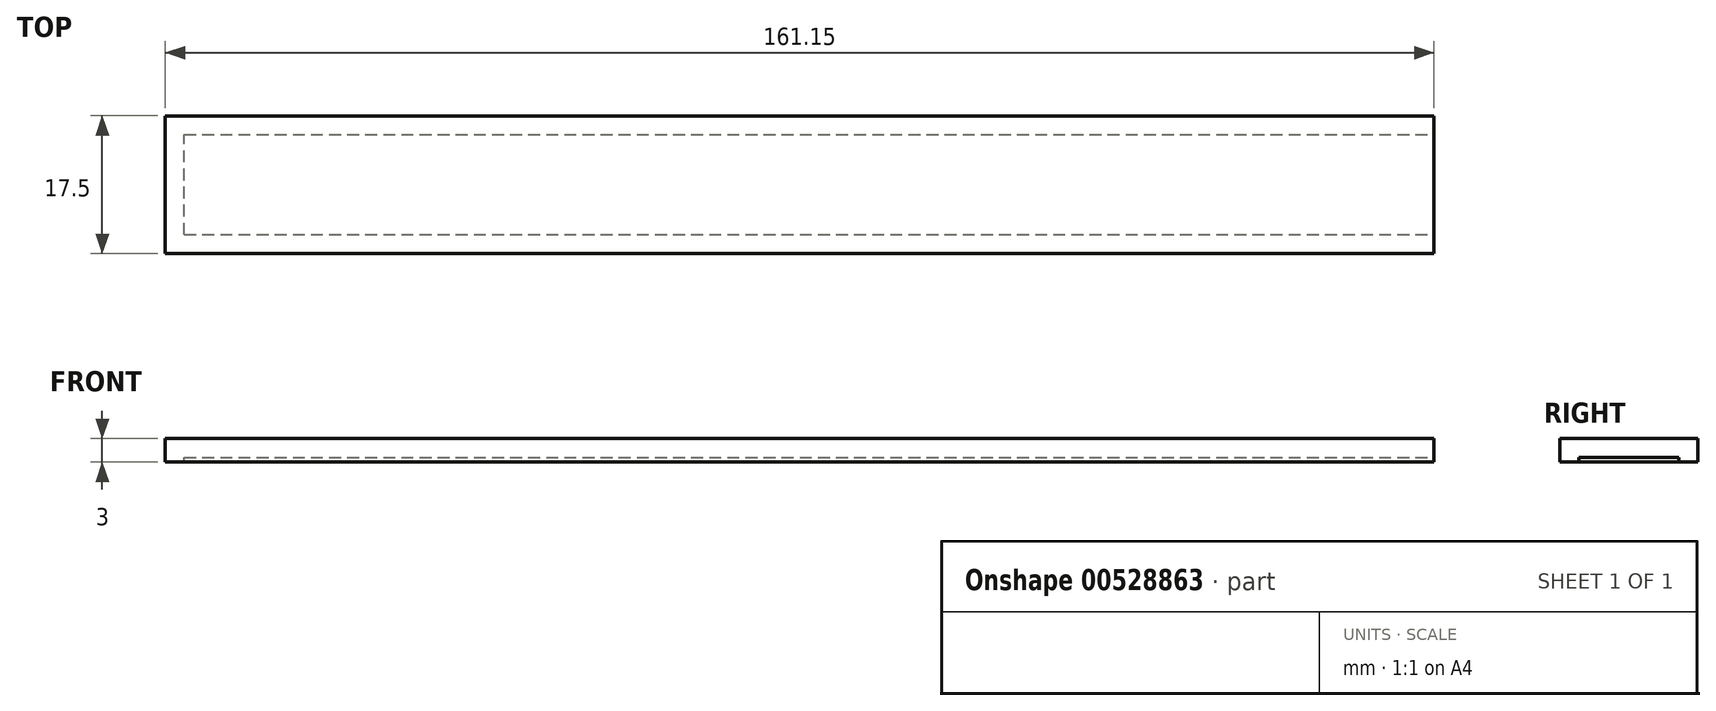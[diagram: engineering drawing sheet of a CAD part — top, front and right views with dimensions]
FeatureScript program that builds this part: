
annotation { "Feature Type Name" : "Feature", "Feature Type Description" : "" }
export const myFeature = defineFeature(function(context is Context, id is Id, definition is map)
    precondition{}
    {
        {
            var Q0;
            Q0=qCreatedBy(makeId("Top.planeOp"),FACE);
            var sketch = newSketch(context, id + "F0", { "sketchPlane" : qUnion([Q0])});
            skLineSegment(sketch, "E0.bottom", {"start": v(154.58, 29.43) * mm, "end": v(-6.57, 29.43) * mm});
            skLineSegment(sketch, "E0.top", {"start": v(154.58, 11.93) * mm, "end": v(-6.57, 11.93) * mm});
            skLineSegment(sketch, "E0.left", {"start": v(154.58, 29.43) * mm, "end": v(154.58, 11.93) * mm});
            skLineSegment(sketch, "E0.right", {"start": v(-6.57, 29.43) * mm, "end": v(-6.57, 11.93) * mm});
            skSolve(sketch);
        }
        {
            var Q0;
            Q0=makeQuery(id+"F0.imprint","IMPRINT",FACE,{"disambiguationData":[TD([[makeQuery(id+"F0.imprint","IMPRINT",EDGE,{"derivedFrom":sQuery(id+"F0.wireOp",EDGE,"E0.bottom")}),1.0]])]});
            extrude(context, id + "F1", {"entities" : qUnion([Q0]), "depth" : 2.4 * mm, "offsetDistance" : 25.4 * mm});
        }
        {
            var Q0;
            Q0=makeQuery(id+"F1.opExtrude","CAP_FACE",FACE,{"disambiguationData":[OSD([sQuery(id+"F0.wireOp",EDGE,"E0.bottom"),sQuery(id+"F0.wireOp",EDGE,"E0.top"),sQuery(id+"F0.wireOp",EDGE,"E0.left"),sQuery(id+"F0.wireOp",EDGE,"E0.right")])],"isStart":true});
            var sketch = newSketch(context, id + "F2", { "sketchPlane" : qUnion([Q0])});
            skLineSegment(sketch, "E1.bottom", {"start": v(-6.57, -29.43) * mm, "end": v(154.58, -29.43) * mm});
            skLineSegment(sketch, "E1.top", {"start": v(-6.57, -27.03) * mm, "end": v(154.58, -27.03) * mm});
            skLineSegment(sketch, "E1.left", {"start": v(-6.57, -29.43) * mm, "end": v(-6.57, -27.03) * mm});
            skLineSegment(sketch, "E1.right", {"start": v(154.58, -29.43) * mm, "end": v(154.58, -27.03) * mm});
            skSolve(sketch);
        }
        {
            var Q0;
            Q0 = qSketchRegion(id + "F2", true);
            extrude(context, id + "F3", {"entities" : qUnion([Q0]), "operationType" : NewBodyOperationType.ADD, "depth" : 0.6 * mm, "offsetDistance" : 25.4 * mm});
        }
        {
            var Q0;
            Q0=makeQuery(id+"F1.opExtrude","CAP_FACE",FACE,{"disambiguationData":[OSD([sQuery(id+"F0.wireOp",EDGE,"E0.bottom"),sQuery(id+"F0.wireOp",EDGE,"E0.top"),sQuery(id+"F0.wireOp",EDGE,"E0.left"),sQuery(id+"F0.wireOp",EDGE,"E0.right")])],"isStart":true});
            var sketch = newSketch(context, id + "F4", { "sketchPlane" : qUnion([Q0])});
            skLineSegment(sketch, "E2.bottom", {"start": v(-6.57, -11.93) * mm, "end": v(154.58, -11.93) * mm});
            skLineSegment(sketch, "E2.top", {"start": v(-6.57, -14.33) * mm, "end": v(154.58, -14.33) * mm});
            skLineSegment(sketch, "E2.left", {"start": v(-6.57, -11.93) * mm, "end": v(-6.57, -14.33) * mm});
            skLineSegment(sketch, "E2.right", {"start": v(154.58, -11.93) * mm, "end": v(154.58, -14.33) * mm});
            skSolve(sketch);
        }
        {
            var Q0;
            Q0 = qSketchRegion(id + "F4", true);
            extrude(context, id + "F5", {"entities" : qUnion([Q0]), "operationType" : NewBodyOperationType.ADD, "depth" : 0.6 * mm, "offsetDistance" : 25.4 * mm});
        }
        {
            var Q0;
            Q0=makeQuery(id+"F1.opExtrude","CAP_FACE",FACE,{"disambiguationData":[OSD([sQuery(id+"F0.wireOp",EDGE,"E0.bottom"),sQuery(id+"F0.wireOp",EDGE,"E0.top"),sQuery(id+"F0.wireOp",EDGE,"E0.left"),sQuery(id+"F0.wireOp",EDGE,"E0.right")])],"isStart":true});
            var sketch = newSketch(context, id + "F6", { "sketchPlane" : qUnion([Q0])});
            skLineSegment(sketch, "E3.bottom", {"start": v(-6.57, -14.33) * mm, "end": v(-4.17, -14.33) * mm});
            skLineSegment(sketch, "E3.top", {"start": v(-6.57, -27.03) * mm, "end": v(-4.17, -27.03) * mm});
            skLineSegment(sketch, "E3.left", {"start": v(-6.57, -14.33) * mm, "end": v(-6.57, -27.03) * mm});
            skLineSegment(sketch, "E3.right", {"start": v(-4.17, -14.33) * mm, "end": v(-4.17, -27.03) * mm});
            skSolve(sketch);
        }
        {
            var Q0;
            Q0 = qSketchRegion(id + "F6", true);
            extrude(context, id + "F7", {"entities" : qUnion([Q0]), "operationType" : NewBodyOperationType.ADD, "depth" : 0.6 * mm, "offsetDistance" : 25.4 * mm});
        }
    });
